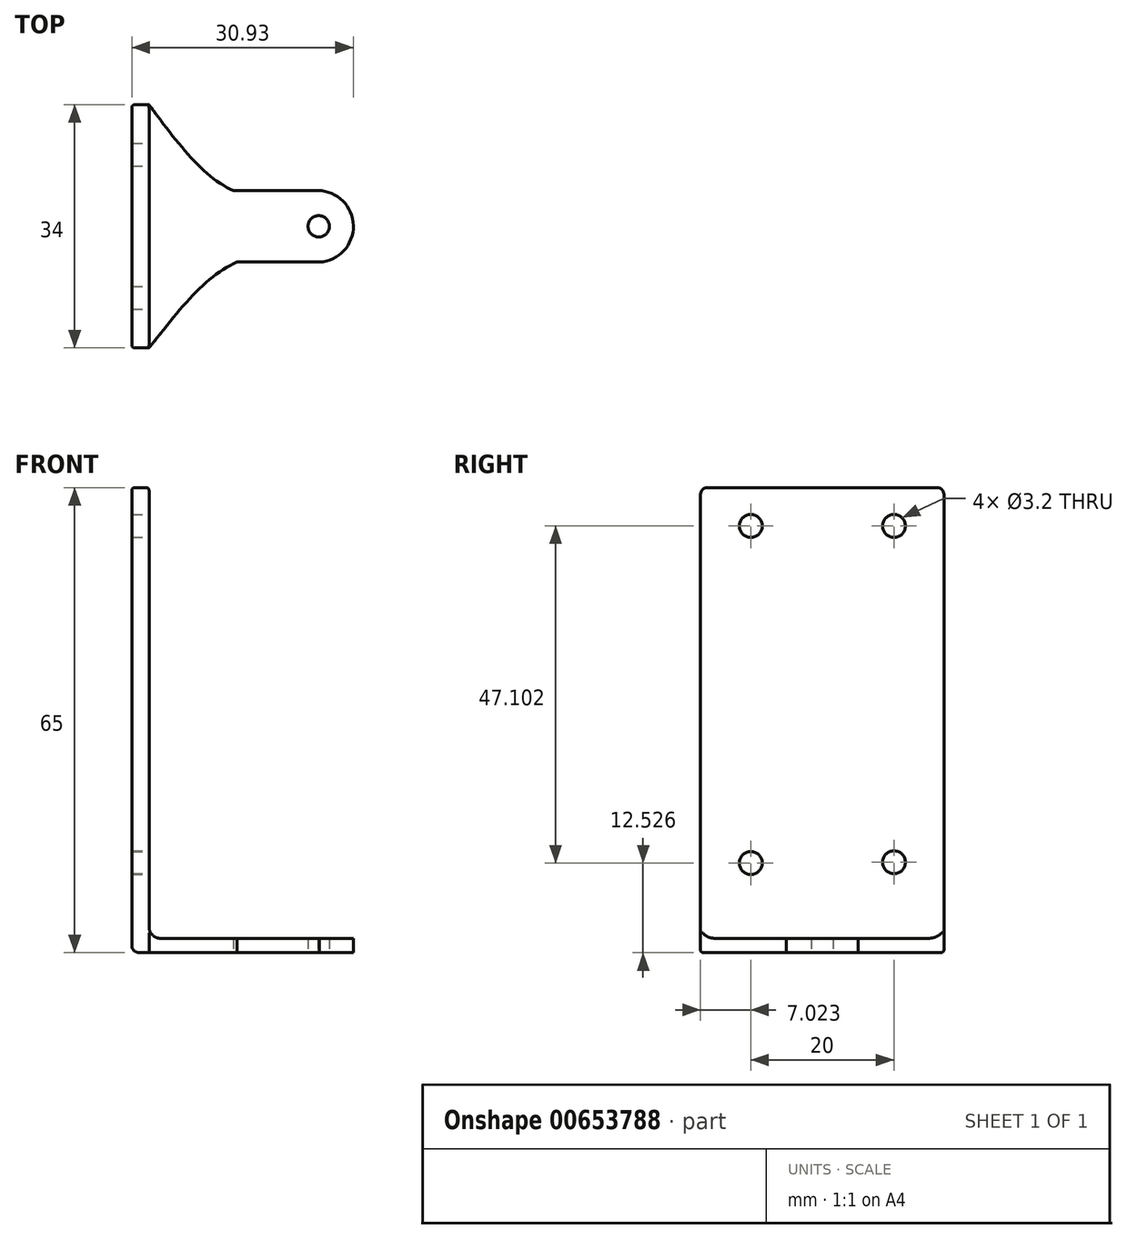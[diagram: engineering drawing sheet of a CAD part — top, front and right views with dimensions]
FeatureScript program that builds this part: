
annotation { "Feature Type Name" : "Feature", "Feature Type Description" : "" }
export const myFeature = defineFeature(function(context is Context, id is Id, definition is map)
    precondition{}
    {
        {
            var Q0;
            Q0=qCreatedBy(makeId("Top.planeOp"),FACE);
            var sketch = newSketch(context, id + "F0", { "sketchPlane" : qUnion([Q0])});
            skLineSegment(sketch, "E0.bottom", {"start": v(13.5, -5) * mm, "end": v(25, -5) * mm});
            skLineSegment(sketch, "E0.top", {"start": v(13, 5) * mm, "end": v(24.8, 5) * mm});
            skCircle(sketch, "E1", {"center": v(24.9, 0) * mm, "radius": 1.5 * mm});
            skArc(sketch, "E2", {"start": v(25, -5) * mm, "mid": v(29.73, 0.1) * mm, "end": v(24.8, 5) * mm});
            skPoint(sketch, "E2.third.point", {"position": v(29.55, 1.35) * mm});
            skLineSegment(sketch, "E3.bottom", {"start": v(-1.2, 17) * mm, "end": v(1.2, 17) * mm});
            skLineSegment(sketch, "E3.top", {"start": v(-1.2, -17) * mm, "end": v(1.2, -17) * mm});
            skLineSegment(sketch, "E3.left", {"start": v(-1.2, 17) * mm, "end": v(-1.2, -17) * mm});
            skLineSegment(sketch, "E3.right", {"start": v(1.2, 17) * mm, "end": v(1.2, -17) * mm});
            skPoint(sketch, "E3.middle", {"position": v(0, 0) * mm});
            skFitSpline(sketch, "E4", {"points": [v(1.2, 17) * mm, v(1.2, 5) * mm], "startDerivative": vector(0, -12) * mm, "endDerivative": vector(0, -12) * mm});
            skFitSpline(sketch, "E5", {"points": [v(1.2, 17) * mm, v(13, 5) * mm, v(24.8, 5) * mm], "startDerivative": vector(20.96, -28.1) * mm, "endDerivative": vector(27.23, 5.05) * mm});
            skFitSpline(sketch, "E6", {"points": [v(1.2, -17) * mm, v(13.5, -5) * mm, v(25, -5) * mm], "startDerivative": vector(21.88, 27.77) * mm, "endDerivative": vector(26.27, -4.89) * mm});
            skSolve(sketch);
        }
        {
            var Q0;
            Q0=qSketchRegion(id+"F0",true);
            extrude(context, id + "F1", {"entities" : qUnion([Q0]), "depth" : 2 * mm, "offsetDistance" : 25 * mm});
        }
        {
            var Q0;
            Q0=makeQuery(id+"F0.imprint","IMPRINT",FACE,{"disambiguationData":[TD([[makeQuery(id+"F0.imprint","IMPRINT",EDGE,{"derivedFrom":sQuery(id+"F0.wireOp",EDGE,"E3.bottom")}),-1.0]])]});
            extrude(context, id + "F2", {"entities" : qUnion([Q0]), "operationType" : NewBodyOperationType.ADD, "depth" : 65 * mm, "offsetDistance" : 25 * mm});
        }
        {
            var Q0;
            Q0=makeQuery(id+"F2.opExtrude","SWEPT_FACE",FACE,{"disambiguationData":[OSD([sQuery(id+"F0.wireOp",EDGE,"E3.right")])]});
            var sketch = newSketch(context, id + "F3", { "sketchPlane" : qUnion([Q0])});
            skCircle(sketch, "E7", {"center": v(-9.98, 59.63) * mm, "radius": 1.6 * mm});
            skCircle(sketch, "E8", {"center": v(10.02, 59.63) * mm, "radius": 1.6 * mm});
            skCircle(sketch, "E9", {"center": v(10.02, 12.63) * mm, "radius": 1.6 * mm});
            skCircle(sketch, "E10", {"center": v(-9.98, 12.53) * mm, "radius": 1.6 * mm});
            skLineSegment(sketch, "E11.bottom", {"start": v(-9.98, 12.63) * mm, "end": v(10.02, 12.63) * mm});
            skLineSegment(sketch, "E11.top", {"start": v(-9.98, 59.63) * mm, "end": v(10.02, 59.63) * mm});
            skLineSegment(sketch, "E11.left", {"start": v(-9.98, 12.63) * mm, "end": v(-9.98, 59.63) * mm});
            skLineSegment(sketch, "E11.right", {"start": v(10.02, 12.63) * mm, "end": v(10.02, 59.63) * mm});
            skSolve(sketch);
        }
        {
            var Q0;
            Q0=makeQuery(id+"F3.imprint","IMPRINT",FACE,{"disambiguationData":[TD([[makeQuery(id+"F3.imprint","IMPRINT",EDGE,{"derivedFrom":sQuery(id+"F3.wireOp",EDGE,"E7")}),1.0]])]});
            var Q1;
            Q1=makeQuery(id+"F3.imprint","IMPRINT",FACE,{"disambiguationData":[TD([[makeQuery(id+"F3.imprint","IMPRINT",EDGE,{"derivedFrom":sQuery(id+"F3.wireOp",EDGE,"E8")}),1.0]])]});
            var Q2;
            Q2=makeQuery(id+"F3.imprint","IMPRINT",FACE,{"disambiguationData":[TD([[makeQuery(id+"F3.imprint","IMPRINT",EDGE,{"derivedFrom":sQuery(id+"F3.wireOp",EDGE,"E9")}),1.0]])]});
            var Q3;
            Q3=makeQuery(id+"F3.imprint","IMPRINT",FACE,{"disambiguationData":[TD([[makeQuery(id+"F3.imprint","IMPRINT",EDGE,{"derivedFrom":sQuery(id+"F3.wireOp",EDGE,"E10")}),1.0]])]});
            extrude(context, id + "F4", {"entities" : qUnion([Q0, Q1, Q2, Q3]), "operationType" : NewBodyOperationType.REMOVE, "oppositeDirection" : true, "depth" : 3 * mm, "offsetDistance" : 25 * mm});
        }
        {
            var Q0;
            Q0=makeQuery(id+"F2.boolean.opBoolean","INTERSECT",EDGE,{"derivedFrom":[makeQuery(id+"F1.opExtrude","CAP_FACE",FACE,{"disambiguationData":[OSD([sQuery(id+"F0.wireOp",EDGE,"E0.bottom"),sQuery(id+"F0.wireOp",EDGE,"E0.top"),sQuery(id+"F0.wireOp",EDGE,"E1"),sQuery(id+"F0.wireOp",EDGE,"E2"),sQuery(id+"F0.wireOp",EDGE,"E3.bottom"),sQuery(id+"F0.wireOp",EDGE,"E3.top"),sQuery(id+"F0.wireOp",EDGE,"E3.left"),sQuery(id+"F0.wireOp",EDGE,"E5"),sQuery(id+"F0.wireOp",EDGE,"E6")])],"isStart":false}),makeQuery(id+"F2.opExtrude","SWEPT_FACE",FACE,{"disambiguationData":[OSD([sQuery(id+"F0.wireOp",EDGE,"E3.right")])]})]});
            fillet(context, id + "F5", {"entities" : qUnion([Q0]), "radius" : 1.6 * mm, "tangentPropagation" : true, "allowEdgeOverflow" : false});
        }
        {
            var Q0;
            Q0=makeQuery(id+"F2.opExtrude","CAP_EDGE",EDGE,{"disambiguationData":[OSD([sQuery(id+"F0.wireOp",EDGE,"E3.top")])],"isStart":false});
            fillet(context, id + "F6", {"entities" : qUnion([Q0]), "radius" : 1 * mm, "tangentPropagation" : true, "allowEdgeOverflow" : false});
        }
        {
            var Q0;
            Q0=makeQuery(id+"F2.opExtrude","CAP_EDGE",EDGE,{"disambiguationData":[OSD([sQuery(id+"F0.wireOp",EDGE,"E3.bottom")])],"isStart":false});
            fillet(context, id + "F7", {"entities" : qUnion([Q0]), "radius" : 1 * mm, "tangentPropagation" : true, "allowEdgeOverflow" : false});
        }
        {
            var Q0;
            Q0=makeQuery(id+"F1.opExtrude","CAP_EDGE",EDGE,{"disambiguationData":[OSD([sQuery(id+"F0.wireOp",EDGE,"E3.left")])],"isStart":true});
            fillet(context, id + "F8", {"entities" : qUnion([Q0]), "radius" : 1 * mm, "tangentPropagation" : true, "allowEdgeOverflow" : false});
        }
        {
            var Q0;
            Q0=makeQuery(id+"F2.opExtrude","SWEPT_EDGE",EDGE,{"disambiguationData":[OSD([sQuery(id+"F0.wireOp",EDGE,"E3.bottom"),sQuery(id+"F0.wireOp",EDGE,"E5"),sQuery(id+"F0.wireOp",EDGE,"E3.right")])]});
            var Q1;
            {var subQ0=sQuery(id+"F0.wireOp",EDGE,"E3.left");var subQ1=sQuery(id+"F0.wireOp",EDGE,"E3.bottom");Q1=makeQuery(id+"F2.boolean.opBoolean","MERGE",EDGE,{"derivedFrom":[makeQuery(id+"F1.opExtrude","SWEPT_EDGE",EDGE,{"disambiguationData":[OSD([subQ1,subQ0])]}),makeQuery(id+"F2.opExtrude","SWEPT_EDGE",EDGE,{"disambiguationData":[OSD([subQ1,subQ0])]})]});}
            var Q2;
            {var subQ0=sQuery(id+"F0.wireOp",EDGE,"E3.left");var subQ1=sQuery(id+"F0.wireOp",EDGE,"E3.top");Q2=makeQuery(id+"F2.boolean.opBoolean","MERGE",EDGE,{"derivedFrom":[makeQuery(id+"F1.opExtrude","SWEPT_EDGE",EDGE,{"disambiguationData":[OSD([subQ1,subQ0])]}),makeQuery(id+"F2.opExtrude","SWEPT_EDGE",EDGE,{"disambiguationData":[OSD([subQ1,subQ0])]})]});}
            var Q3;
            Q3=makeQuery(id+"F2.opExtrude","SWEPT_EDGE",EDGE,{"disambiguationData":[OSD([sQuery(id+"F0.wireOp",EDGE,"E3.top"),sQuery(id+"F0.wireOp",EDGE,"E6"),sQuery(id+"F0.wireOp",EDGE,"E3.right")])]});
            fillet(context, id + "F9", {"entities" : qUnion([Q0, Q1, Q2, Q3]), "radius" : 0.4 * mm, "tangentPropagation" : true, "allowEdgeOverflow" : false});
        }
    });
